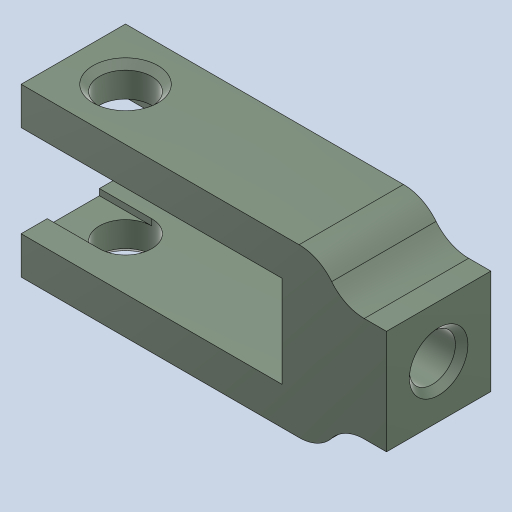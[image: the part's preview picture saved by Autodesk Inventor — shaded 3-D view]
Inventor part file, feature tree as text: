
AUTODESK INVENTOR PART (.ipt)
format: ipt  version: 2023 (Build 270158000, 158)  size: 213,504 bytes
history: native  units: mm
features: sketch x5, extrude x4, fillet x2, chamfer x2, other x1, hole x1
ambient origin geometry x8: Origin, YZ Plane, XZ Plane, XY Plane, X Axis, Y Axis, Z Axis, Center Point
bodies: Body1 (feature_tree)
feature tree (15):
  other  "ソリッド1"
  extrude  "押し出し1"  Depth=2.5mm
  extrude  "押し出し5"  Depth=2.5mm
  extrude  "押し出し3"  Depth=12.0mm
  extrude  "押し出し4"  Depth=8.0mm TaperAngle=0.0deg
  hole  "穴3"  [1 undecoded]
  fillet  "フィレット2"  Radius=3.0mm
  chamfer  "面取り1"  Distance=2.0mm
  chamfer  "面取り2"  Distance=5.0mm
  fillet  "フィレット4"  Radius=3.0mm
  sketch  "スケッチ1"
  sketch  "スケッチ3"
  sketch  "スケッチ5"
  sketch  "スケッチ7"
  sketch  "スケッチ8"
note: 1 required parameter value undecoded (feature->parameter linkage not recoverable at this tier; creation-order binding heuristic only, values carry confidence <= 0.55)
